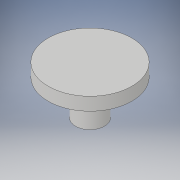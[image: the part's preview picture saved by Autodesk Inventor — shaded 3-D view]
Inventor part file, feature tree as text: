
AUTODESK INVENTOR PART (.ipt)
format: ipt  version: 2019.4 (Build 234330000, 330)  size: 145,408 bytes
history: native  units: in
note: dims shown in document units (in); Inventor stores cm internally (conversion verified against a paired STEP export)
features: sketch x5, extrude x3, hole x2
ambient origin geometry x8: Origin, YZ Plane, XZ Plane, XY Plane, X Axis, Y Axis, Z Axis, Center Point
bodies: Solid1 (feature_tree)
feature tree (10):
  extrude  "Extrusion1"  Depth=0.3925in TaperAngle=0.0deg
  extrude  "Extrusion3"  Depth=0.0752in TaperAngle=0.0deg
  hole  "Hole2"  [1 undecoded]
  extrude  "Extrusion4"  Depth=1.1811in TaperAngle=360.0deg
  hole  "Hole3"  [1 undecoded]
  sketch  "Sketch1"  dims[d0=2.0457in d1=0.3925in d2=0.0in]
  sketch  "Sketch4"  dims[d18=1.7488in d19=0.0752in d20=0.0in]
  sketch  "Sketch6"  dims[d21=1.4961in d22=0.1201in]
  sketch  "Sketch7"  dims[d24=0.748in d25=1.1811in d27=360.0deg]
  sketch  "Sketch8"  dims[d29=0.1201in d30=0.2362in d31=0.119in d32=0.0787in d33=0.5635in d34=0.1969in d35=0.8108in d36=0.7087in d37=0.7886in d38=0.0in d39=0.1181in d40=0.1575in d41=0.1575in d42=1.5748in d44=360.0deg d46=0.0968in d47=0.2362in d48=0.119in d49=0.0787in d50=0.5635in d51=0.3465in d52=0.8108in]
note: 2 required parameter values undecoded (feature->parameter linkage not recoverable at this tier; creation-order binding heuristic only, values carry confidence <= 0.55)
